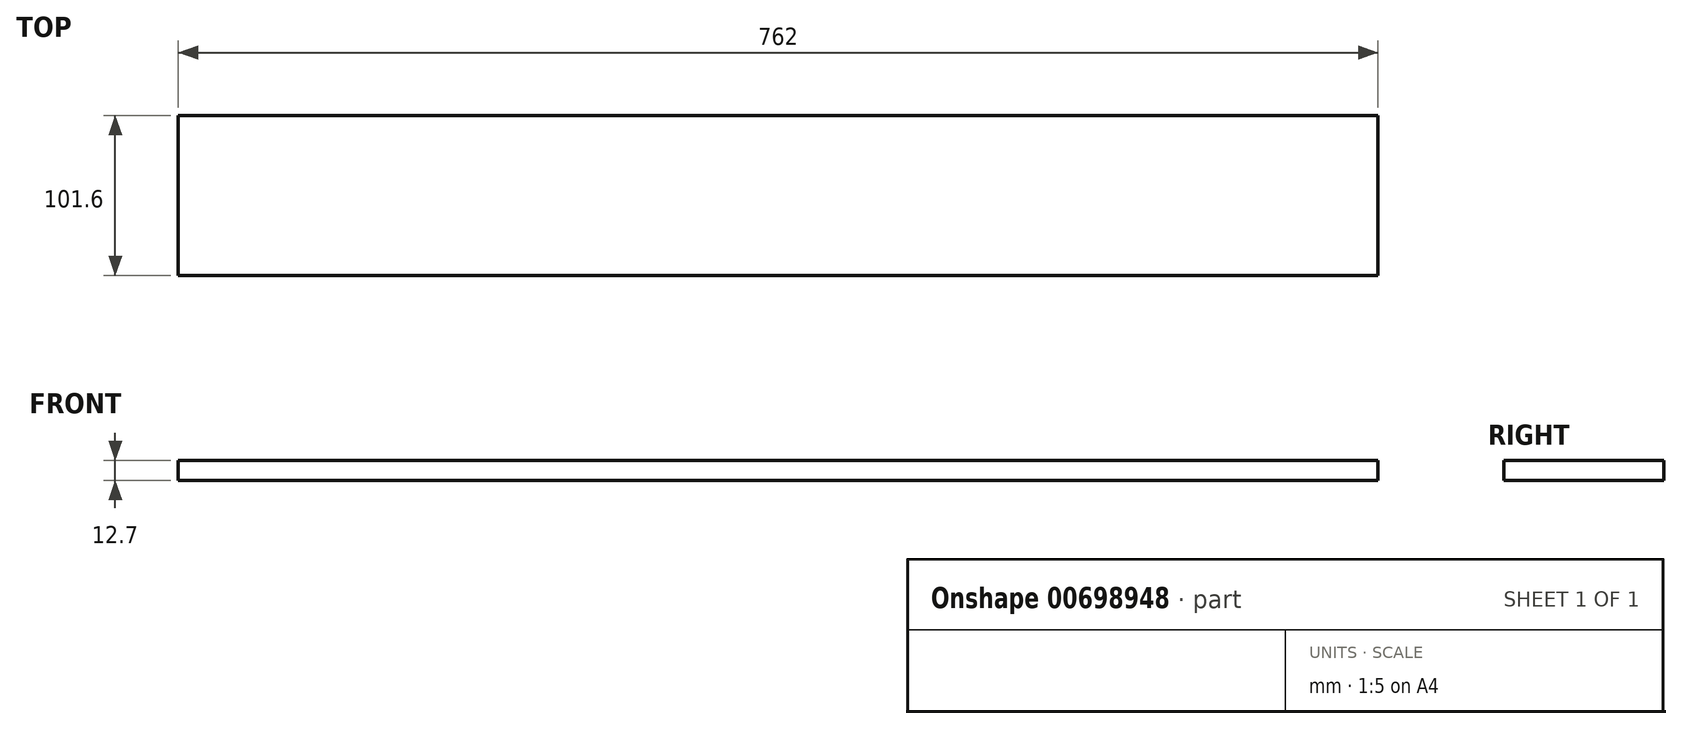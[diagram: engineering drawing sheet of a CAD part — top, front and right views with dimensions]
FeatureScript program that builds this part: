
annotation { "Feature Type Name" : "Feature", "Feature Type Description" : "" }
export const myFeature = defineFeature(function(context is Context, id is Id, definition is map)
    precondition{}
    {
        {
            var Q0;
            Q0=qCreatedBy(makeId("Top.planeOp"),FACE);
            var sketch = newSketch(context, id + "F0", { "sketchPlane" : qUnion([Q0])});
            skLineSegment(sketch, "E0.bottom", {"start": v(258.82, -68.98) * mm, "end": v(-503.18, -68.98) * mm});
            skLineSegment(sketch, "E0.top", {"start": v(258.82, -170.58) * mm, "end": v(-503.18, -170.58) * mm});
            skLineSegment(sketch, "E0.left", {"start": v(258.82, -68.98) * mm, "end": v(258.82, -170.58) * mm});
            skLineSegment(sketch, "E0.right", {"start": v(-503.18, -68.98) * mm, "end": v(-503.18, -170.58) * mm});
            skSolve(sketch);
        }
        {
            var Q0;
            Q0=makeQuery(id+"F0.imprint","IMPRINT",FACE,{"disambiguationData":[TD([[makeQuery(id+"F0.imprint","IMPRINT",EDGE,{"derivedFrom":sQuery(id+"F0.wireOp",EDGE,"E0.bottom")}),1.0]])]});
            extrude(context, id + "F1", {"entities" : qUnion([Q0]), "depth" : 12.7 * mm, "offsetDistance" : 25.4 * mm});
        }
    });
